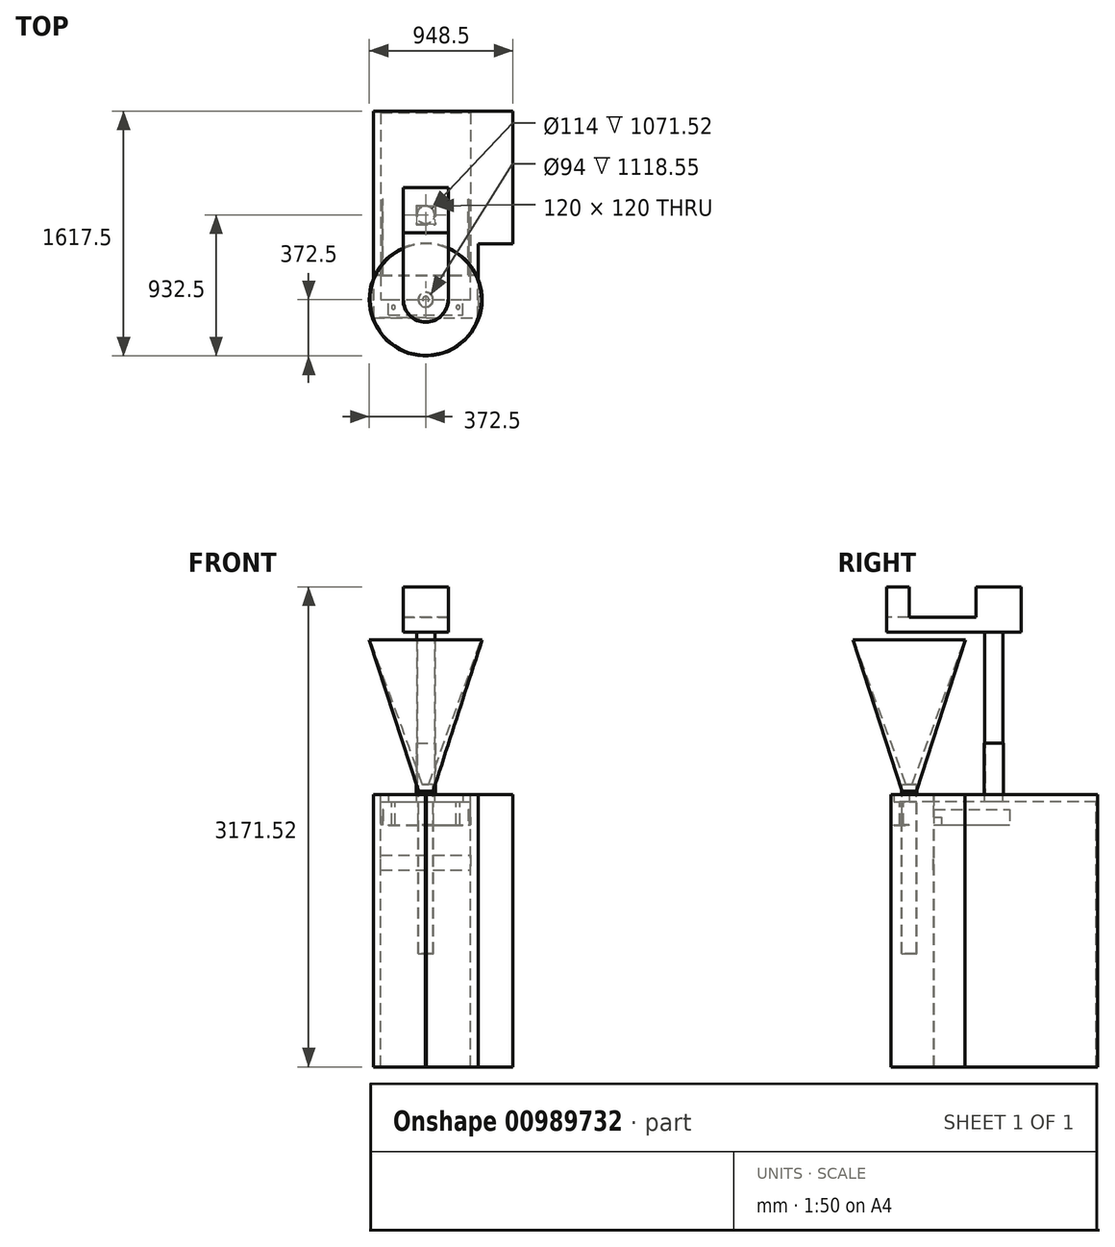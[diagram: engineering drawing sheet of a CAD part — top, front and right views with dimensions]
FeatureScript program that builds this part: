
annotation { "Feature Type Name" : "Feature", "Feature Type Description" : "" }
export const myFeature = defineFeature(function(context is Context, id is Id, definition is map)
    precondition{}
    {
        {
            var Q0;
            Q0=qCreatedBy(makeId("Top.planeOp"),FACE);
            var sketch = newSketch(context, id + "F0", { "sketchPlane" : qUnion([Q0])});
            skLineSegment(sketch, "E0.bottom", {"start": v(231, -672.5) * mm, "end": v(-461, -672.5) * mm});
            skLineSegment(sketch, "E0.top", {"start": v(461, 672.5) * mm, "end": v(-461, 672.5) * mm});
            skLineSegment(sketch, "E0.left", {"start": v(461, -202.5) * mm, "end": v(461, 672.5) * mm});
            skLineSegment(sketch, "E0.right", {"start": v(-461, -672.5) * mm, "end": v(-461, 672.5) * mm});
            skPoint(sketch, "E0.middle", {"position": v(0, 0) * mm});
            skLineSegment(sketch, "E1", {"start": v(-461, -202.5) * mm, "end": v(461, -202.5) * mm});
            skLineSegment(sketch, "E2", {"start": v(231, -202.5) * mm, "end": v(231, -672.5) * mm});
            skPoint(sketch, "E3.orphan", {"position": v(461, -672.5) * mm});
            skSolve(sketch);
        }
        {
            var Q0;
            {var subQ4=sQuery(id+"F0.wireOp",EDGE,"E0.top");Q0=makeQuery(id+"F0.imprint","IMPRINT",FACE,{"disambiguationData":[TD([[makeQuery(id+"F0.imprint","IMPRINT",EDGE,{"derivedFrom":subQ4}),1.0]])]});}
            var Q1;
            {var subQ0=sQuery(id+"F0.wireOp",EDGE,"E0.bottom");Q1=makeQuery(id+"F0.imprint","IMPRINT",FACE,{"disambiguationData":[TD([[makeQuery(id+"F0.imprint","IMPRINT",EDGE,{"derivedFrom":subQ0}),-1.0]])]});}
            extrude(context, id + "F1", {"entities" : qUnion([Q0, Q1]), "oppositeDirection" : true, "depth" : 1800 * mm, "offsetDistance" : 25.4 * mm});
        }
        {
            var Q0;
            Q0=makeQuery(id+"F1.opExtrude","CAP_FACE",FACE,{"disambiguationData":[OSD([sQuery(id+"F0.wireOp",EDGE,"E0.bottom"),sQuery(id+"F0.wireOp",EDGE,"E0.top"),sQuery(id+"F0.wireOp",EDGE,"E0.left"),sQuery(id+"F0.wireOp",EDGE,"E0.right"),sQuery(id+"F0.wireOp",EDGE,"E1"),sQuery(id+"F0.wireOp",EDGE,"E2")])],"isStart":true});
            var sketch = newSketch(context, id + "F2", { "sketchPlane" : qUnion([Q0])});
            skLineSegment(sketch, "E4", {"start": v(-461, -409.9) * mm, "end": v(-411, -409.9) * mm});
            skLineSegment(sketch, "E5", {"start": v(-411, -409.9) * mm, "end": v(-411, -572.5) * mm});
            skLineSegment(sketch, "E6", {"start": v(-411, -572.5) * mm, "end": v(181, -572.5) * mm});
            skLineSegment(sketch, "E7", {"start": v(181, -572.5) * mm, "end": v(181, -409.9) * mm});
            skLineSegment(sketch, "E8", {"start": v(181, -409.9) * mm, "end": v(231, -409.9) * mm});
            skLineSegment(sketch, "E9", {"start": v(-461, -409.9) * mm, "end": v(-461, -672.5) * mm});
            skLineSegment(sketch, "E10", {"start": v(-461, -672.5) * mm, "end": v(231, -672.5) * mm});
            skLineSegment(sketch, "E11", {"start": v(231, -672.5) * mm, "end": v(231, -409.9) * mm});
            skLineSegment(sketch, "E12", {"start": v(-115, -234.95) * mm, "end": v(-115, -672.5) * mm, "construction": true});
            skPoint(sketch, "E12.startSnap0", {"position": v(-115, -572.5) * mm});
            skSolve(sketch);
        }
        {
            var Q0;
            Q0 = qSketchRegion(id + "F2", true);
            extrude(context, id + "F3", {"entities" : qUnion([Q0]), "operationType" : NewBodyOperationType.REMOVE, "endBound" : BoundingType.UP_TO_NEXT, "oppositeDirection" : true, "depth" : 25.4 * mm, "offsetDistance" : 25.4 * mm});
        }
        {
            var Q0;
            Q0=makeQuery(id+"F3.boolean.opBoolean","COPY",FACE,{"derivedFrom":makeQuery(id+"F3.opExtrude","SWEPT_FACE",FACE,{"disambiguationData":[OSD([sQuery(id+"F2.wireOp",EDGE,"E6")])]})});
            var sketch = newSketch(context, id + "F4", { "sketchPlane" : qUnion([Q0])});
            skLineSegment(sketch, "E13.bottom", {"start": v(-411, -50) * mm, "end": v(181, -50) * mm});
            skLineSegment(sketch, "E13.top", {"start": v(-411, -1800) * mm, "end": v(181, -1800) * mm});
            skLineSegment(sketch, "E13.left", {"start": v(-411, -50) * mm, "end": v(-411, -1800) * mm});
            skLineSegment(sketch, "E13.right", {"start": v(181, -50) * mm, "end": v(181, -1800) * mm});
            skSolve(sketch);
        }
        {
            var Q0;
            Q0 = qSketchRegion(id + "F4", true);
            extrude(context, id + "F5", {"entities" : qUnion([Q0]), "operationType" : NewBodyOperationType.REMOVE, "oppositeDirection" : true, "depth" : 1335 * mm - 100 * mm, "offsetDistance" : 25.4 * mm});
        }
        {
            var Q0;
            Q0=makeQuery(id+"F1.opExtrude","CAP_FACE",FACE,{"disambiguationData":[OSD([sQuery(id+"F0.wireOp",EDGE,"E0.bottom"),sQuery(id+"F0.wireOp",EDGE,"E0.top"),sQuery(id+"F0.wireOp",EDGE,"E0.left"),sQuery(id+"F0.wireOp",EDGE,"E0.right"),sQuery(id+"F0.wireOp",EDGE,"E1"),sQuery(id+"F0.wireOp",EDGE,"E2")])],"isStart":true});
            var sketch = newSketch(context, id + "F6", { "sketchPlane" : qUnion([Q0])});
            skLineSegment(sketch, "E14.bottom", {"start": v(-175, 47.5) * mm, "end": v(-55, 47.5) * mm});
            skLineSegment(sketch, "E14.top", {"start": v(-175, -72.5) * mm, "end": v(-55, -72.5) * mm});
            skLineSegment(sketch, "E14.left", {"start": v(-175, 47.5) * mm, "end": v(-175, -72.5) * mm});
            skLineSegment(sketch, "E14.right", {"start": v(-55, 47.5) * mm, "end": v(-55, -72.5) * mm});
            skLineSegment(sketch, "E15", {"start": v(-115, -572.5) * mm, "end": v(-115, 207.32) * mm, "construction": true});
            skSolve(sketch);
        }
        {
            var Q0;
            Q0 = qSketchRegion(id + "F6", true);
            extrude(context, id + "F7", {"entities" : qUnion([Q0]), "operationType" : NewBodyOperationType.REMOVE, "endBound" : BoundingType.UP_TO_NEXT, "oppositeDirection" : true, "depth" : 25.4 * mm, "offsetDistance" : 25.4 * mm});
        }
        {
            var Q0;
            Q0=makeQuery(id+"F1.opExtrude","CAP_FACE",FACE,{"disambiguationData":[OSD([sQuery(id+"F0.wireOp",EDGE,"E0.bottom"),sQuery(id+"F0.wireOp",EDGE,"E0.top"),sQuery(id+"F0.wireOp",EDGE,"E0.left"),sQuery(id+"F0.wireOp",EDGE,"E0.right"),sQuery(id+"F0.wireOp",EDGE,"E1"),sQuery(id+"F0.wireOp",EDGE,"E2")])],"isStart":true});
            var sketch = newSketch(context, id + "F8", { "sketchPlane" : qUnion([Q0])});
            skLineSegment(sketch, "E16.bottom", {"start": v(-178, 50.5) * mm, "end": v(-52, 50.5) * mm});
            skLineSegment(sketch, "E16.top", {"start": v(-178, -75.5) * mm, "end": v(-52, -75.5) * mm});
            skLineSegment(sketch, "E16.left", {"start": v(-178, 50.5) * mm, "end": v(-178, -75.5) * mm});
            skLineSegment(sketch, "E16.right", {"start": v(-52, 50.5) * mm, "end": v(-52, -75.5) * mm});
            skLineSegment(sketch, "E17.bottom", {"start": v(-175, 47.5) * mm, "end": v(-55, 47.5) * mm});
            skLineSegment(sketch, "E17.top", {"start": v(-175, -72.5) * mm, "end": v(-55, -72.5) * mm});
            skLineSegment(sketch, "E17.left", {"start": v(-175, 47.5) * mm, "end": v(-175, -72.5) * mm});
            skLineSegment(sketch, "E17.right", {"start": v(-55, 47.5) * mm, "end": v(-55, -72.5) * mm});
            skSolve(sketch);
        }
        {
            var Q0;
            Q0 = qSketchRegion(id + "F8", true);
            extrude(context, id + "F9", {"entities" : qUnion([Q0]), "operationType" : NewBodyOperationType.ADD, "depth" : 340 * mm, "offsetDistance" : 25.4 * mm});
        }
        {
            var Q0;
            Q0=makeQuery(id+"F9.opExtrude","CAP_FACE",FACE,{"disambiguationData":[OSD([sQuery(id+"F8.wireOp",EDGE,"E16.bottom"),sQuery(id+"F8.wireOp",EDGE,"E16.top"),sQuery(id+"F8.wireOp",EDGE,"E16.left"),sQuery(id+"F8.wireOp",EDGE,"E16.right"),sQuery(id+"F8.wireOp",EDGE,"E17.bottom"),sQuery(id+"F8.wireOp",EDGE,"E17.top"),sQuery(id+"F8.wireOp",EDGE,"E17.left"),sQuery(id+"F8.wireOp",EDGE,"E17.right")])],"isStart":false});
            var sketch = newSketch(context, id + "F10", { "sketchPlane" : qUnion([Q0])});
            skCircle(sketch, "E18", {"center": v(-115, -12.5) * mm, "radius": 60 * mm});
            skPoint(sketch, "E18.centerSnap0", {"position": v(-175, -12.5) * mm});
            skPoint(sketch, "E18.centerSnap1", {"position": v(-115, -75.5) * mm});
            skCircle(sketch, "E19", {"center": v(-115, -12.5) * mm, "radius": 57 * mm});
            skSolve(sketch);
        }
        {
            var Q0;
            Q0 = qSketchRegion(id + "F10", true);
            extrude(context, id + "F11", {"entities" : qUnion([Q0]), "depth" : 731.52 * mm, "offsetDistance" : 25.4 * mm, "hasSecondDirection" : true, "secondDirectionOppositeDirection" : true, "secondDirectionDepth" : 340 * mm});
        }
        {
            var Q0;
            Q0=makeQuery(id+"F3.boolean.opBoolean","COPY",FACE,{"derivedFrom":makeQuery(id+"F3.opExtrude","SWEPT_FACE",FACE,{"disambiguationData":[OSD([sQuery(id+"F2.wireOp",EDGE,"E6")])]})});
            var sketch = newSketch(context, id + "F12", { "sketchPlane" : qUnion([Q0])});
            skLineSegment(sketch, "E20.bottom", {"start": v(-361, 0) * mm, "end": v(131, 0) * mm});
            skLineSegment(sketch, "E20.top", {"start": v(-361, -50) * mm, "end": v(131, -50) * mm});
            skLineSegment(sketch, "E20.left", {"start": v(-361, 0) * mm, "end": v(-361, -50) * mm});
            skLineSegment(sketch, "E20.right", {"start": v(131, 0) * mm, "end": v(131, -50) * mm});
            skSolve(sketch);
        }
        {
            var Q0;
            Q0 = qSketchRegion(id + "F12", true);
            extrude(context, id + "F13", {"entities" : qUnion([Q0]), "operationType" : NewBodyOperationType.ADD, "depth" : 100 * mm, "offsetDistance" : 25.4 * mm});
        }
        {
            var Q0;
            Q0=makeQuery(id+"F13.boolean.opBoolean","MERGE",FACE,{"derivedFrom":[makeQuery(id+"F1.opExtrude","CAP_FACE",FACE,{"disambiguationData":[OSD([sQuery(id+"F0.wireOp",EDGE,"E0.bottom"),sQuery(id+"F0.wireOp",EDGE,"E0.top"),sQuery(id+"F0.wireOp",EDGE,"E0.left"),sQuery(id+"F0.wireOp",EDGE,"E0.right"),sQuery(id+"F0.wireOp",EDGE,"E1"),sQuery(id+"F0.wireOp",EDGE,"E2")])],"isStart":true}),makeQuery(id+"F13.opExtrude","SWEPT_FACE",FACE,{"disambiguationData":[OSD([sQuery(id+"F12.wireOp",EDGE,"E20.bottom")])]})]});
            var sketch = newSketch(context, id + "F14", { "sketchPlane" : qUnion([Q0])});
            skCircle(sketch, "E21", {"center": v(-115, -572.5) * mm, "radius": 50 * mm});
            skPoint(sketch, "E21.centerSnap0", {"position": v(-115, -672.5) * mm});
            skSolve(sketch);
        }
        {
            var Q0;
            Q0 = qSketchRegion(id + "F14", true);
            extrude(context, id + "F15", {"entities" : qUnion([Q0]), "operationType" : NewBodyOperationType.REMOVE, "endBound" : BoundingType.UP_TO_NEXT, "oppositeDirection" : true, "depth" : 25.4 * mm, "offsetDistance" : 25.4 * mm});
        }
        {
            var Q0;
            Q0=makeQuery(id+"F13.boolean.opBoolean","MERGE",FACE,{"derivedFrom":[makeQuery(id+"F1.opExtrude","CAP_FACE",FACE,{"disambiguationData":[OSD([sQuery(id+"F0.wireOp",EDGE,"E0.bottom"),sQuery(id+"F0.wireOp",EDGE,"E0.top"),sQuery(id+"F0.wireOp",EDGE,"E0.left"),sQuery(id+"F0.wireOp",EDGE,"E0.right"),sQuery(id+"F0.wireOp",EDGE,"E1"),sQuery(id+"F0.wireOp",EDGE,"E2")])],"isStart":true}),makeQuery(id+"F13.opExtrude","SWEPT_FACE",FACE,{"disambiguationData":[OSD([sQuery(id+"F12.wireOp",EDGE,"E20.bottom")])]})]});
            var sketch = newSketch(context, id + "F16", { "sketchPlane" : qUnion([Q0])});
            skCircle(sketch, "E22", {"center": v(-115, -572.5) * mm, "radius": 50 * mm});
            skCircle(sketch, "E23", {"center": v(-115, -572.5) * mm, "radius": 47 * mm});
            skSolve(sketch);
        }
        {
            var Q0;
            Q0 = qSketchRegion(id + "F16", true);
            extrude(context, id + "F17", {"entities" : qUnion([Q0]), "operationType" : NewBodyOperationType.ADD, "oppositeDirection" : true, "depth" : 1051.56 * mm, "offsetDistance" : 25.4 * mm, "hasSecondDirection" : true, "secondDirectionOppositeDirection" : false, "secondDirectionDepth" : 20 * mm});
        }
        {
            var Q0;
            Q0=makeQuery(id+"F5.boolean.opBoolean","COPY",FACE,{"derivedFrom":makeQuery(id+"F5.opExtrude","SWEPT_FACE",FACE,{"disambiguationData":[OSD([sQuery(id+"F4.wireOp",EDGE,"E13.left")])]})});
            var sketch = newSketch(context, id + "F18", { "sketchPlane" : qUnion([Q0])});
            skLineSegment(sketch, "E24.bottom", {"start": v(-409.9, -150) * mm, "end": v(-359.9, -150) * mm});
            skLineSegment(sketch, "E24.top", {"start": v(-409.9, -200) * mm, "end": v(-359.9, -200) * mm});
            skLineSegment(sketch, "E24.left", {"start": v(-409.9, -150) * mm, "end": v(-409.9, -200) * mm});
            skLineSegment(sketch, "E24.right", {"start": v(-359.9, -150) * mm, "end": v(-359.9, -200) * mm});
            skSolve(sketch);
        }
        {
            var Q0;
            Q0 = qSketchRegion(id + "F18", true);
            extrude(context, id + "F19", {"entities" : qUnion([Q0]), "operationType" : NewBodyOperationType.ADD, "depth" : 10 * mm, "offsetDistance" : 25.4 * mm});
        }
        {
            var Q0;
            Q0=makeQuery(id+"F5.boolean.opBoolean","COPY",FACE,{"derivedFrom":makeQuery(id+"F5.opExtrude","SWEPT_FACE",FACE,{"disambiguationData":[OSD([sQuery(id+"F4.wireOp",EDGE,"E13.right")])]})});
            var sketch = newSketch(context, id + "F20", { "sketchPlane" : qUnion([Q0])});
            skLineSegment(sketch, "E25.bottom", {"start": v(409.9, -150) * mm, "end": v(359.9, -150) * mm});
            skLineSegment(sketch, "E25.top", {"start": v(409.9, -200) * mm, "end": v(359.9, -200) * mm});
            skLineSegment(sketch, "E25.left", {"start": v(409.9, -150) * mm, "end": v(409.9, -200) * mm});
            skLineSegment(sketch, "E25.right", {"start": v(359.9, -150) * mm, "end": v(359.9, -200) * mm});
            skSolve(sketch);
        }
        {
            var Q0;
            Q0 = qSketchRegion(id + "F20", true);
            extrude(context, id + "F21", {"entities" : qUnion([Q0]), "operationType" : NewBodyOperationType.ADD, "depth" : 10 * mm, "offsetDistance" : 25.4 * mm});
        }
        {
            var Q0;
            Q0=makeQuery(id+"F19.opExtrude","CAP_FACE",FACE,{"disambiguationData":[OSD([sQuery(id+"F18.wireOp",EDGE,"E24.bottom"),sQuery(id+"F18.wireOp",EDGE,"E24.top"),sQuery(id+"F18.wireOp",EDGE,"E24.left"),sQuery(id+"F18.wireOp",EDGE,"E24.right")])],"isStart":false});
            var sketch = newSketch(context, id + "F22", { "sketchPlane" : qUnion([Q0])});
            skLineSegment(sketch, "E26.bottom", {"start": v(-409.9, -100) * mm, "end": v(90.1, -100) * mm});
            skLineSegment(sketch, "E26.top", {"start": v(-409.9, -200) * mm, "end": v(90.1, -200) * mm});
            skLineSegment(sketch, "E26.left", {"start": v(-409.9, -100) * mm, "end": v(-409.9, -200) * mm});
            skLineSegment(sketch, "E26.right", {"start": v(90.1, -100) * mm, "end": v(90.1, -200) * mm});
            skSolve(sketch);
        }
        {
            var Q0;
            Q0 = qSketchRegion(id + "F22", true);
            extrude(context, id + "F23", {"entities" : qUnion([Q0]), "operationType" : NewBodyOperationType.ADD, "depth" : 5 * mm, "offsetDistance" : 25.4 * mm});
        }
        {
            var Q0;
            Q0=makeQuery(id+"F21.opExtrude","CAP_FACE",FACE,{"disambiguationData":[OSD([sQuery(id+"F20.wireOp",EDGE,"E25.bottom"),sQuery(id+"F20.wireOp",EDGE,"E25.top"),sQuery(id+"F20.wireOp",EDGE,"E25.left"),sQuery(id+"F20.wireOp",EDGE,"E25.right")])],"isStart":false});
            var sketch = newSketch(context, id + "F24", { "sketchPlane" : qUnion([Q0])});
            skLineSegment(sketch, "E27.bottom", {"start": v(409.9, -100) * mm, "end": v(-90.1, -100) * mm});
            skLineSegment(sketch, "E27.top", {"start": v(409.9, -200) * mm, "end": v(-90.1, -200) * mm});
            skLineSegment(sketch, "E27.left", {"start": v(409.9, -100) * mm, "end": v(409.9, -200) * mm});
            skLineSegment(sketch, "E27.right", {"start": v(-90.1, -100) * mm, "end": v(-90.1, -200) * mm});
            skSolve(sketch);
        }
        {
            var Q0;
            Q0 = qSketchRegion(id + "F24", true);
            extrude(context, id + "F25", {"entities" : qUnion([Q0]), "operationType" : NewBodyOperationType.ADD, "depth" : 5 * mm, "offsetDistance" : 25.4 * mm});
        }
        {
            var Q0;
            Q0=makeQuery(id+"F23.boolean.opBoolean","MERGE",FACE,{"derivedFrom":[makeQuery(id+"F19.boolean.opBoolean","MERGE",FACE,{"derivedFrom":[makeQuery(id+"F3.boolean.opBoolean","COPY",FACE,{"derivedFrom":makeQuery(id+"F3.opExtrude","SWEPT_FACE",FACE,{"disambiguationData":[OSD([sQuery(id+"F2.wireOp",EDGE,"E4")])]})}),makeQuery(id+"F19.opExtrude","SWEPT_FACE",FACE,{"disambiguationData":[OSD([sQuery(id+"F18.wireOp",EDGE,"E24.left")])]})]}),makeQuery(id+"F23.opExtrude","SWEPT_FACE",FACE,{"disambiguationData":[OSD([sQuery(id+"F22.wireOp",EDGE,"E26.left")])]})]});
            var sketch = newSketch(context, id + "F26", { "sketchPlane" : qUnion([Q0])});
            skLineSegment(sketch, "E28.bottom", {"start": v(-411, -400) * mm, "end": v(181, -400) * mm});
            skLineSegment(sketch, "E28.top", {"start": v(-411, -500) * mm, "end": v(181, -500) * mm});
            skLineSegment(sketch, "E28.left", {"start": v(-411, -400) * mm, "end": v(-411, -500) * mm});
            skLineSegment(sketch, "E28.right", {"start": v(181, -400) * mm, "end": v(181, -500) * mm});
            skSolve(sketch);
        }
        {
            var Q0;
            Q0 = qSketchRegion(id + "F26", true);
            extrude(context, id + "F27", {"entities" : qUnion([Q0]), "depth" : 5 * mm, "offsetDistance" : 25.4 * mm});
        }
        {
            var Q0;
            Q0=makeQuery(id+"F13.boolean.opBoolean","MERGE",FACE,{"derivedFrom":[makeQuery(id+"F5.boolean.opBoolean","COPY",FACE,{"derivedFrom":makeQuery(id+"F5.opExtrude","SWEPT_FACE",FACE,{"disambiguationData":[OSD([sQuery(id+"F4.wireOp",EDGE,"E13.bottom")])]})}),makeQuery(id+"F13.opExtrude","SWEPT_FACE",FACE,{"disambiguationData":[OSD([sQuery(id+"F12.wireOp",EDGE,"E20.top")])]})]});
            var sketch = newSketch(context, id + "F28", { "sketchPlane" : qUnion([Q0])});
            skCircle(sketch, "E29", {"center": v(-328.5, 622.5) * mm, "radius": 12.5 * mm});
            skPoint(sketch, "E29.centerSnap0", {"position": v(-361, 622.5) * mm});
            skCircle(sketch, "E30", {"center": v(98.5, 622.5) * mm, "radius": 12.5 * mm});
            skPoint(sketch, "E30.centerSnap0", {"position": v(131, 622.5) * mm});
            skSolve(sketch);
        }
        {
            var Q0;
            Q0 = qSketchRegion(id + "F28", true);
            extrude(context, id + "F29", {"entities" : qUnion([Q0]), "operationType" : NewBodyOperationType.ADD, "depth" : 150 * mm, "offsetDistance" : 25.4 * mm});
        }
        {
            var Q0;
            Q0=makeQuery(id+"F29.opExtrude","CAP_FACE",FACE,{"disambiguationData":[OSD([sQuery(id+"F28.wireOp",EDGE,"E29")])],"isStart":false});
            var sketch = newSketch(context, id + "F30", { "sketchPlane" : qUnion([Q0])});
            skLineSegment(sketch, "E31.bottom", {"start": v(-361, 672.5) * mm, "end": v(131, 672.5) * mm});
            skLineSegment(sketch, "E31.top", {"start": v(-361, 572.5) * mm, "end": v(-165, 572.5) * mm});
            skLineSegment(sketch, "E31.left", {"start": v(-361, 672.5) * mm, "end": v(-361, 572.5) * mm});
            skLineSegment(sketch, "E31.right", {"start": v(131, 672.5) * mm, "end": v(131, 572.5) * mm});
            skArc(sketch, "E32", {"start": v(-65, 572.5) * mm, "mid": v(-115, 622.5) * mm, "end": v(-165, 572.5) * mm});
            skLineSegment(sketch, "E33.trimOffspring", {"start": v(-65, 572.5) * mm, "end": v(131, 572.5) * mm});
            skSolve(sketch);
        }
        {
            var Q0;
            Q0 = qSketchRegion(id + "F30", true);
            extrude(context, id + "F31", {"entities" : qUnion([Q0]), "operationType" : NewBodyOperationType.ADD, "depth" : 3 * mm, "offsetDistance" : 25.4 * mm});
        }
        {
            var Q0;
            Q0=makeQuery(id+"F17.opExtrude","CAP_FACE",FACE,{"disambiguationData":[OSD([sQuery(id+"F16.wireOp",EDGE,"E22"),sQuery(id+"F16.wireOp",EDGE,"E23")])],"isStart":true});
            cPlane(context, id + "F32", {"entities" : qUnion([Q0]), "cplaneType" : CPlaneType.OFFSET, "offset" : 1000 * mm, "width" : 152.4 * mm, "height" : 152.4 * mm});
        }
        {
            var Q0;
            Q0=qCreatedBy(id+"F32.planeOp",FACE);
            var sketch = newSketch(context, id + "F33", { "sketchPlane" : qUnion([Q0])});
            skCircle(sketch, "E34", {"center": v(-115, -572.5) * mm, "radius": 372.5 * mm});
            skSolve(sketch);
        }
        {
            var Q0;
            Q0 = qSketchRegion(id + "F33", true);
            var Q1;
            Q1=makeQuery(id+"F17.opExtrude","CAP_FACE",FACE,{"disambiguationData":[OSD([sQuery(id+"F16.wireOp",EDGE,"E22"),sQuery(id+"F16.wireOp",EDGE,"E23")])],"isStart":true});
            extrude(context, id + "F34", {"entities" : qUnion([Q0]), "operationType" : NewBodyOperationType.ADD, "endBound" : BoundingType.UP_TO_SURFACE, "oppositeDirection" : true, "depth" : 25.4 * mm, "endBoundEntityFace" : qUnion([Q1]), "offsetDistance" : 25.4 * mm, "hasDraft" : true, "draftAngle" : 18 * degree, "draftPullDirection" : true});
        }
        {
            var Q0;
            Q0=makeQuery(id+"F34.opExtrude","CAP_FACE",FACE,{"disambiguationData":[OSD([sQuery(id+"F33.wireOp",EDGE,"E34")])],"isStart":true});
            var sketch = newSketch(context, id + "F35", { "sketchPlane" : qUnion([Q0])});
            skCircle(sketch, "E35", {"center": v(-115, -572.5) * mm, "radius": 367.5 * mm});
            skSolve(sketch);
        }
        {
            var Q0;
            Q0 = qSketchRegion(id + "F35", true);
            extrude(context, id + "F36", {"entities" : qUnion([Q0]), "operationType" : NewBodyOperationType.REMOVE, "oppositeDirection" : true, "depth" : 1002.28 * mm, "offsetDistance" : 25.4 * mm, "hasDraft" : true, "draftAngle" : 20 * degree, "draftPullDirection" : true});
        }
        {
            var Q0;
            Q0=makeQuery(id+"F34.opExtrude","CAP_FACE",FACE,{"disambiguationData":[OSD([sQuery(id+"F33.wireOp",EDGE,"E34")])],"isStart":false});
            var sketch = newSketch(context, id + "F37", { "sketchPlane" : qUnion([Q0])});
            skCircle(sketch, "E36", {"center": v(-115, 572.5) * mm, "radius": 47 * mm});
            skSolve(sketch);
        }
        {
            var Q0;
            Q0 = qSketchRegion(id + "F37", true);
            extrude(context, id + "F38", {"entities" : qUnion([Q0]), "operationType" : NewBodyOperationType.REMOVE, "oppositeDirection" : true, "depth" : 47 * mm, "offsetDistance" : 25.4 * mm});
        }
        {
            var Q0;
            Q0=makeQuery(id+"F11.opExtrude","CAP_FACE",FACE,{"disambiguationData":[OSD([sQuery(id+"F10.wireOp",EDGE,"E18"),sQuery(id+"F10.wireOp",EDGE,"E19")])],"isStart":false});
            var sketch = newSketch(context, id + "F39", { "sketchPlane" : qUnion([Q0])});
            skLineSegment(sketch, "E37.bottom", {"start": v(-265, 168.21) * mm, "end": v(35, 168.21) * mm});
            skLineSegment(sketch, "E37.left", {"start": v(-265, 168.21) * mm, "end": v(-265, -231.79) * mm});
            skLineSegment(sketch, "E37.right", {"start": v(35, 168.21) * mm, "end": v(35, -231.79) * mm});
            skArc(sketch, "E38", {"start": v(-265, -572.5) * mm, "mid": v(-115, -722.5) * mm, "end": v(35, -572.5) * mm});
            skLineSegment(sketch, "E39", {"start": v(35, -231.79) * mm, "end": v(35, -572.5) * mm});
            skLineSegment(sketch, "E40", {"start": v(-265, -231.79) * mm, "end": v(-265, -572.5) * mm});
            skSolve(sketch);
        }
        {
            var Q0;
            Q0 = qSketchRegion(id + "F39", true);
            extrude(context, id + "F40", {"entities" : qUnion([Q0]), "operationType" : NewBodyOperationType.ADD, "depth" : 100 * mm, "offsetDistance" : 25.4 * mm});
        }
        {
            var Q0;
            Q0=makeQuery(id+"F40.opExtrude","CAP_FACE",FACE,{"disambiguationData":[OSD([sQuery(id+"F39.wireOp",EDGE,"E37.bottom"),sQuery(id+"F39.wireOp",EDGE,"E37.left"),sQuery(id+"F39.wireOp",EDGE,"E37.right"),sQuery(id+"F39.wireOp",EDGE,"E38"),sQuery(id+"F39.wireOp",EDGE,"E39"),sQuery(id+"F39.wireOp",EDGE,"E40")])],"isStart":false});
            var sketch = newSketch(context, id + "F41", { "sketchPlane" : qUnion([Q0])});
            skLineSegment(sketch, "E41.bottom", {"start": v(35, 168.21) * mm, "end": v(-265, 168.21) * mm});
            skLineSegment(sketch, "E41.top", {"start": v(35, -131.79) * mm, "end": v(-265, -131.79) * mm});
            skLineSegment(sketch, "E41.left", {"start": v(35, 168.21) * mm, "end": v(35, -131.79) * mm});
            skLineSegment(sketch, "E41.right", {"start": v(-265, 168.21) * mm, "end": v(-265, -131.79) * mm});
            skSolve(sketch);
        }
        {
            var Q0;
            Q0 = qSketchRegion(id + "F41", true);
            extrude(context, id + "F42", {"entities" : qUnion([Q0]), "operationType" : NewBodyOperationType.ADD, "depth" : 200 * mm, "offsetDistance" : 25.4 * mm});
        }
        {
            var Q0;
            Q0=makeQuery(id+"F40.opExtrude","CAP_FACE",FACE,{"disambiguationData":[OSD([sQuery(id+"F39.wireOp",EDGE,"E37.bottom"),sQuery(id+"F39.wireOp",EDGE,"E37.left"),sQuery(id+"F39.wireOp",EDGE,"E37.right"),sQuery(id+"F39.wireOp",EDGE,"E38"),sQuery(id+"F39.wireOp",EDGE,"E39"),sQuery(id+"F39.wireOp",EDGE,"E40")])],"isStart":false});
            var sketch = newSketch(context, id + "F43", { "sketchPlane" : qUnion([Q0])});
            skArc(sketch, "E42", {"start": v(-265, -572.5) * mm, "mid": v(-115, -722.5) * mm, "end": v(35, -572.5) * mm});
            skLineSegment(sketch, "E43", {"start": v(35, -572.5) * mm, "end": v(32, -572.5) * mm});
            skLineSegment(sketch, "E44", {"start": v(-265, -572.5) * mm, "end": v(-262, -572.5) * mm});
            skArc(sketch, "E45", {"start": v(-262, -572.5) * mm, "mid": v(-115, -719.5) * mm, "end": v(32, -572.5) * mm});
            skSolve(sketch);
        }
        {
            var Q0;
            Q0 = qSketchRegion(id + "F43", true);
            extrude(context, id + "F44", {"entities" : qUnion([Q0]), "operationType" : NewBodyOperationType.ADD, "depth" : 200 * mm, "offsetDistance" : 25.4 * mm});
        }
        {
            var Q0;
            Q0=makeQuery(id+"F23.boolean.opBoolean","MERGE",FACE,{"derivedFrom":[makeQuery(id+"F19.boolean.opBoolean","MERGE",FACE,{"derivedFrom":[makeQuery(id+"F3.boolean.opBoolean","COPY",FACE,{"derivedFrom":makeQuery(id+"F3.opExtrude","SWEPT_FACE",FACE,{"disambiguationData":[OSD([sQuery(id+"F2.wireOp",EDGE,"E4")])]})}),makeQuery(id+"F19.opExtrude","SWEPT_FACE",FACE,{"disambiguationData":[OSD([sQuery(id+"F18.wireOp",EDGE,"E24.left")])]})]}),makeQuery(id+"F23.opExtrude","SWEPT_FACE",FACE,{"disambiguationData":[OSD([sQuery(id+"F22.wireOp",EDGE,"E26.left")])]})]});
            var sketch = newSketch(context, id + "F45", { "sketchPlane" : qUnion([Q0])});
            skLineSegment(sketch, "E46.bottom", {"start": v(-461, 0) * mm, "end": v(-458, 0) * mm});
            skLineSegment(sketch, "E46.top", {"start": v(-461, -1800) * mm, "end": v(-458, -1800) * mm});
            skLineSegment(sketch, "E46.left", {"start": v(-461, 0) * mm, "end": v(-461, -1800) * mm});
            skLineSegment(sketch, "E46.right", {"start": v(-458, 0) * mm, "end": v(-458, -1800) * mm});
            skSolve(sketch);
        }
        {
            var Q0;
            Q0=makeQuery(id+"F25.boolean.opBoolean","MERGE",FACE,{"derivedFrom":[makeQuery(id+"F21.boolean.opBoolean","MERGE",FACE,{"derivedFrom":[makeQuery(id+"F3.boolean.opBoolean","COPY",FACE,{"derivedFrom":makeQuery(id+"F3.opExtrude","SWEPT_FACE",FACE,{"disambiguationData":[OSD([sQuery(id+"F2.wireOp",EDGE,"E8")])]})}),makeQuery(id+"F21.opExtrude","SWEPT_FACE",FACE,{"disambiguationData":[OSD([sQuery(id+"F20.wireOp",EDGE,"E25.left")])]})]}),makeQuery(id+"F25.opExtrude","SWEPT_FACE",FACE,{"disambiguationData":[OSD([sQuery(id+"F24.wireOp",EDGE,"E27.left")])]})]});
            var sketch = newSketch(context, id + "F46", { "sketchPlane" : qUnion([Q0])});
            skLineSegment(sketch, "E47.bottom", {"start": v(231, 0) * mm, "end": v(228, 0) * mm});
            skLineSegment(sketch, "E47.top", {"start": v(231, -1800) * mm, "end": v(228, -1800) * mm});
            skLineSegment(sketch, "E47.left", {"start": v(231, 0) * mm, "end": v(231, -1800) * mm});
            skLineSegment(sketch, "E47.right", {"start": v(228, 0) * mm, "end": v(228, -1800) * mm});
            skSolve(sketch);
        }
        {
            var Q0;
            Q0 = qSketchRegion(id + "F46", true);
            var Q1;
            Q1 = qSketchRegion(id + "F45", true);
            extrude(context, id + "F47", {"entities" : qUnion([Q0, Q1]), "operationType" : NewBodyOperationType.ADD, "depth" : 284.48 * mm, "offsetDistance" : 25.4 * mm});
        }
        {
            var Q0;
            Q0=makeQuery(id+"F47.opExtrude","SWEPT_FACE",FACE,{"disambiguationData":[OSD([sQuery(id+"F45.wireOp",EDGE,"E46.right")])]});
            var sketch = newSketch(context, id + "F48", { "sketchPlane" : qUnion([Q0])});
            skLineSegment(sketch, "E48.bottom", {"start": v(-694.38, 0) * mm, "end": v(-691.38, 0) * mm});
            skLineSegment(sketch, "E48.top", {"start": v(-694.38, -1800) * mm, "end": v(-691.38, -1800) * mm});
            skLineSegment(sketch, "E48.left", {"start": v(-694.38, 0) * mm, "end": v(-694.38, -1800) * mm});
            skLineSegment(sketch, "E48.right", {"start": v(-691.38, 0) * mm, "end": v(-691.38, -1800) * mm});
            skSolve(sketch);
        }
        {
            var Q0;
            Q0 = qSketchRegion(id + "F48", true);
            extrude(context, id + "F49", {"entities" : qUnion([Q0]), "operationType" : NewBodyOperationType.ADD, "depth" : 340.36 * mm, "offsetDistance" : 25.4 * mm});
        }
        {
            var Q0;
            Q0=makeQuery(id+"F47.opExtrude","SWEPT_FACE",FACE,{"disambiguationData":[OSD([sQuery(id+"F46.wireOp",EDGE,"E47.right")])]});
            var sketch = newSketch(context, id + "F50", { "sketchPlane" : qUnion([Q0])});
            skLineSegment(sketch, "E49.bottom", {"start": v(694.38, 0) * mm, "end": v(691.38, 0) * mm});
            skLineSegment(sketch, "E49.top", {"start": v(694.38, -1800) * mm, "end": v(691.38, -1800) * mm});
            skLineSegment(sketch, "E49.left", {"start": v(694.38, 0) * mm, "end": v(694.38, -1800) * mm});
            skLineSegment(sketch, "E49.right", {"start": v(691.38, 0) * mm, "end": v(691.38, -1800) * mm});
            skSolve(sketch);
        }
        {
            var Q0;
            Q0 = qSketchRegion(id + "F50", true);
            var Q1;
            Q1=makeQuery(id+"F49.opExtrude","CAP_FACE",FACE,{"disambiguationData":[OSD([sQuery(id+"F48.wireOp",EDGE,"E48.bottom"),sQuery(id+"F48.wireOp",EDGE,"E48.top"),sQuery(id+"F48.wireOp",EDGE,"E48.left"),sQuery(id+"F48.wireOp",EDGE,"E48.right")])],"isStart":false});
            extrude(context, id + "F51", {"entities" : qUnion([Q0]), "operationType" : NewBodyOperationType.ADD, "depth" : 340.36 * mm, "endBoundEntityFace" : qUnion([Q1]), "offsetDistance" : 25.4 * mm});
        }
    });
